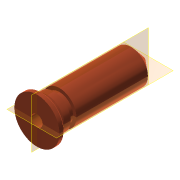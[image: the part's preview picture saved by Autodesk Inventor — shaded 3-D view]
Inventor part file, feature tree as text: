
AUTODESK INVENTOR PART (.ipt)
format: ipt  version: 2016 (Build 200138000, 138)  size: 175,104 bytes
history: native  units: mm
features: sketch x6, extrude x3, revolve x3, chamfer x1
ambient origin geometry x8: Origin, YZ Plane, XZ Plane, XY Plane, X Axis, Y Axis, Z Axis, Center Point
bodies: Solid1 (feature_tree)
feature tree (13):
  extrude  "Extrusion1"  Depth=1.0mm TaperAngle=0.0deg
  extrude  "Extrusion2"  Depth=15.668mm TaperAngle=0.0deg
  extrude  "Extrusion3"  Depth=2.0mm TaperAngle=0.0deg
  revolve  "Revolution1"  [1 undecoded]
  revolve  "Revolution2"  Angle=90.0deg
  chamfer  "Chamfer1"  Angle=90.0deg  [1 undecoded]
  revolve  "Revolution3"  Angle=45.0deg
  sketch  "Sketch1"  dims[d0=8.0mm d1=1.0mm d2=0.0mm]
  sketch  "Sketch2"  dims[d3=6.0mm d4=15.668mm d5=0.0mm]
  sketch  "Sketch3"  dims[d6=2.0mm d7=21.0mm d8=0.0mm]
  sketch  "Sketch4"  dims[d9=6.981317mm d10=0.2mm]
  sketch  "Sketch5"  dims[d11=30.0deg d13=90.0deg]
  sketch  "Sketch6"  dims[d14=0.7mm d15=90.0deg d16=0.3mm d17=2.0mm d18=45.0deg d19=45.0deg d20=0.05mm d21=0.4mm d22=0.05mm d23=0.6mm d24=1.0mm d25=3.0mm d26=90.0deg]
note: 2 required parameter values undecoded (feature->parameter linkage not recoverable at this tier; creation-order binding heuristic only, values carry confidence <= 0.55)